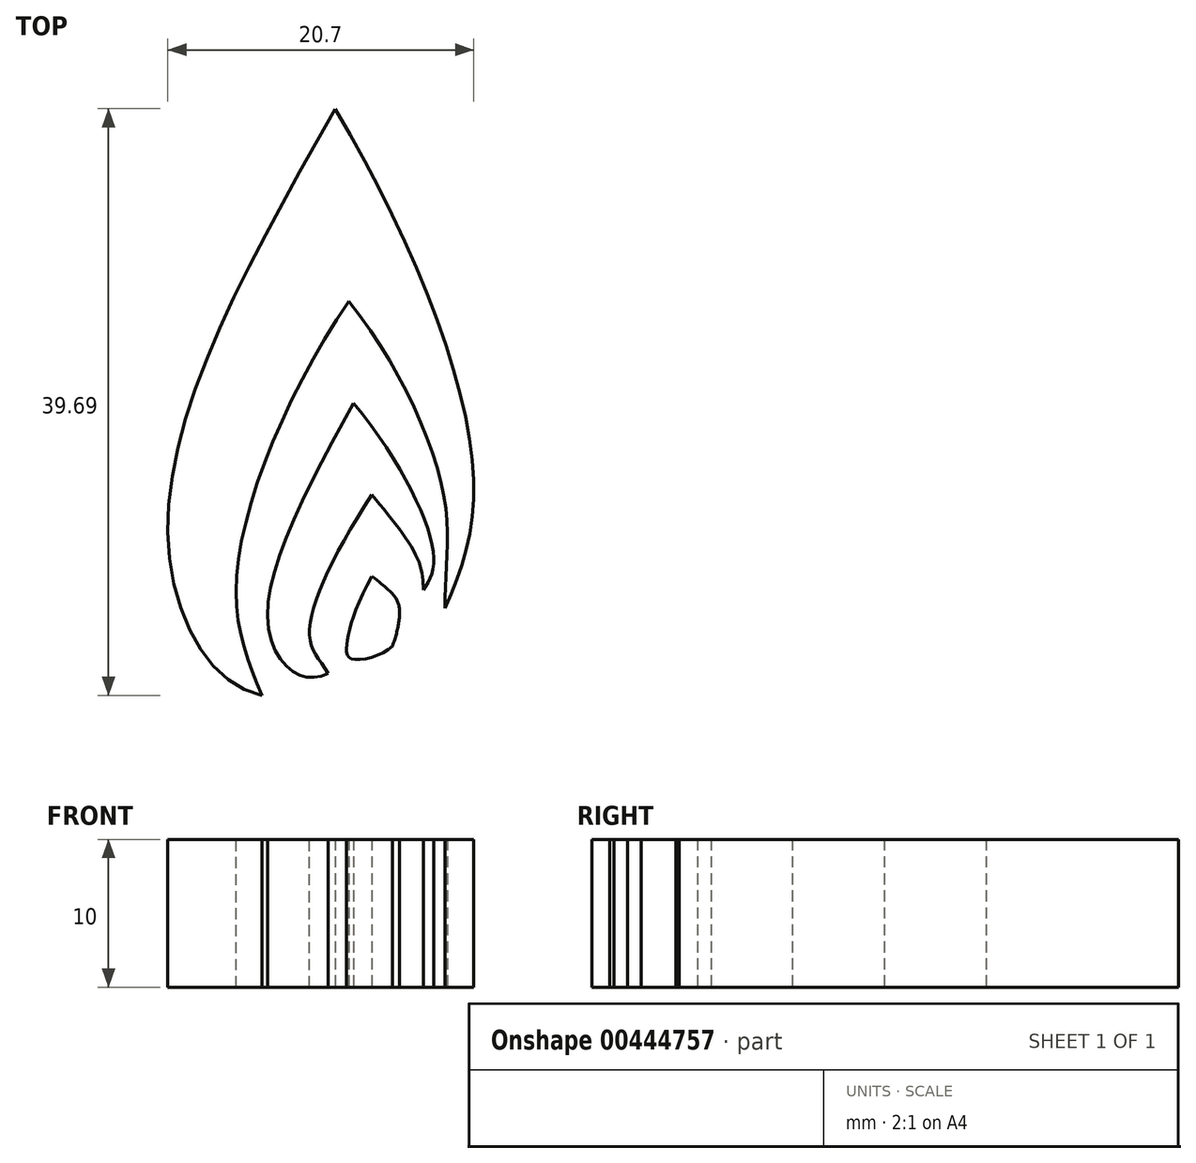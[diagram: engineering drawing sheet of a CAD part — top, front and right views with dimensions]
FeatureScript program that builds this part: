
annotation { "Feature Type Name" : "Feature", "Feature Type Description" : "" }
export const myFeature = defineFeature(function(context is Context, id is Id, definition is map)
    precondition{}
    {
        {
            var Q0;
            Q0=qCreatedBy(makeId("Top.planeOp"),FACE);
            var sketch = newSketch(context, id + "F0", { "sketchPlane" : qUnion([Q0])});
            skFitSpline(sketch, "E0", {"points": [v(-52.36, 18.78) * mm, v(-63.67, -9.82) * mm, v(-57.32, -20.9) * mm], "startDerivative": vector(-27.53, -48.95) * mm, "endDerivative": vector(28.48, -5.93) * mm});
            skFitSpline(sketch, "E1", {"points": [v(-52.36, 18.78) * mm, v(-43.05, -5.25) * mm, v(-44.91, -15.02) * mm], "startDerivative": vector(23.87, -40.28) * mm, "endDerivative": vector(-9.88, -21.62) * mm});
            skFitSpline(sketch, "E2", {"points": [v(-51.43, 5.76) * mm, v(-59.02, -12.85) * mm, v(-57.32, -20.9) * mm], "startDerivative": vector(-19.45, -28.33) * mm, "endDerivative": vector(7.65, -18.73) * mm});
            skFitSpline(sketch, "E3", {"points": [v(-51.43, 5.76) * mm, v(-44.91, -7.96) * mm, v(-44.91, -15.02) * mm], "startDerivative": vector(17.3, -21.93) * mm, "endDerivative": vector(0.59, -16.47) * mm});
            skFitSpline(sketch, "E4", {"points": [v(-51.12, -1.14) * mm, v(-56.93, -15.72) * mm, v(-55, -19.44) * mm, v(-52.82, -19.44) * mm], "startDerivative": vector(-16.87, -30.75) * mm, "endDerivative": vector(11.3, 5.07) * mm});
            skFitSpline(sketch, "E5", {"points": [v(-51.12, -1.14) * mm, v(-45.69, -11.6) * mm, v(-46.39, -13.78) * mm], "startDerivative": vector(14.06, -17.08) * mm, "endDerivative": vector(-3.83, -5.89) * mm});
            skFitSpline(sketch, "E6", {"points": [v(-49.88, -7.34) * mm, v(-54.1, -16.88) * mm, v(-52.82, -19.44) * mm], "startDerivative": vector(-12.05, -18.42) * mm, "endDerivative": vector(5.41, -8.8) * mm});
            skFitSpline(sketch, "E7", {"points": [v(-49.88, -7.34) * mm, v(-46.77, -11.68) * mm, v(-46.39, -13.78) * mm], "startDerivative": vector(6.3, -7.6) * mm, "endDerivative": vector(0.22, -5.08) * mm});
            skFitSpline(sketch, "E8", {"points": [v(-49.88, -12.85) * mm, v(-51.58, -17.65) * mm, v(-51.27, -18.43) * mm, v(-48.48, -17.58) * mm, v(-48.01, -15.02) * mm], "startDerivative": vector(-10.7, -19.39) * mm, "endDerivative": vector(-0.77, 11.4) * mm});
            skFitSpline(sketch, "E9", {"points": [v(-49.88, -12.85) * mm, v(-48.01, -15.02) * mm, v(-48.48, -17.58) * mm], "startDerivative": vector(8.18, -6.36) * mm, "endDerivative": vector(-2.07, -5.48) * mm});
            skSolve(sketch);
        }
        {
            var Q0;
            Q0=makeQuery(id+"F0.imprint","IMPRINT",FACE,{"disambiguationData":[TD([[makeQuery(id+"F0.imprint","IMPRINT",EDGE,{"derivedFrom":sQuery(id+"F0.wireOp",EDGE,"E0")}),1.0]])]});
            var Q1;
            Q1=makeQuery(id+"F0.imprint","IMPRINT",FACE,{"disambiguationData":[TD([[makeQuery(id+"F0.imprint","IMPRINT",EDGE,{"derivedFrom":sQuery(id+"F0.wireOp",EDGE,"E4")}),1.0]])]});
            var Q2;
            {var subQ0=sQuery(id+"F0.wireOp",EDGE,"E9");var subQ1=sQuery(id+"F0.wireOp",EDGE,"E8");var subQ2=makeQuery(id+"F0.imprint","INTERSECT",VERTEX,{"disambiguationData":[OD(0.0)],"derivedFrom":[subQ1,subQ0]});Q2=makeQuery(id+"F0.imprint","IMPRINT",FACE,{"disambiguationData":[TD([[makeQuery(id+"F0.imprint","IMPRINT",EDGE,{"disambiguationData":[TD([[subQ2,-1.0]])],"derivedFrom":subQ1}),1.0]])]});}
            extrude(context, id + "F1", {"entities" : qUnion([Q0, Q1, Q2]), "depth" : 10 * mm});
        }
    });
